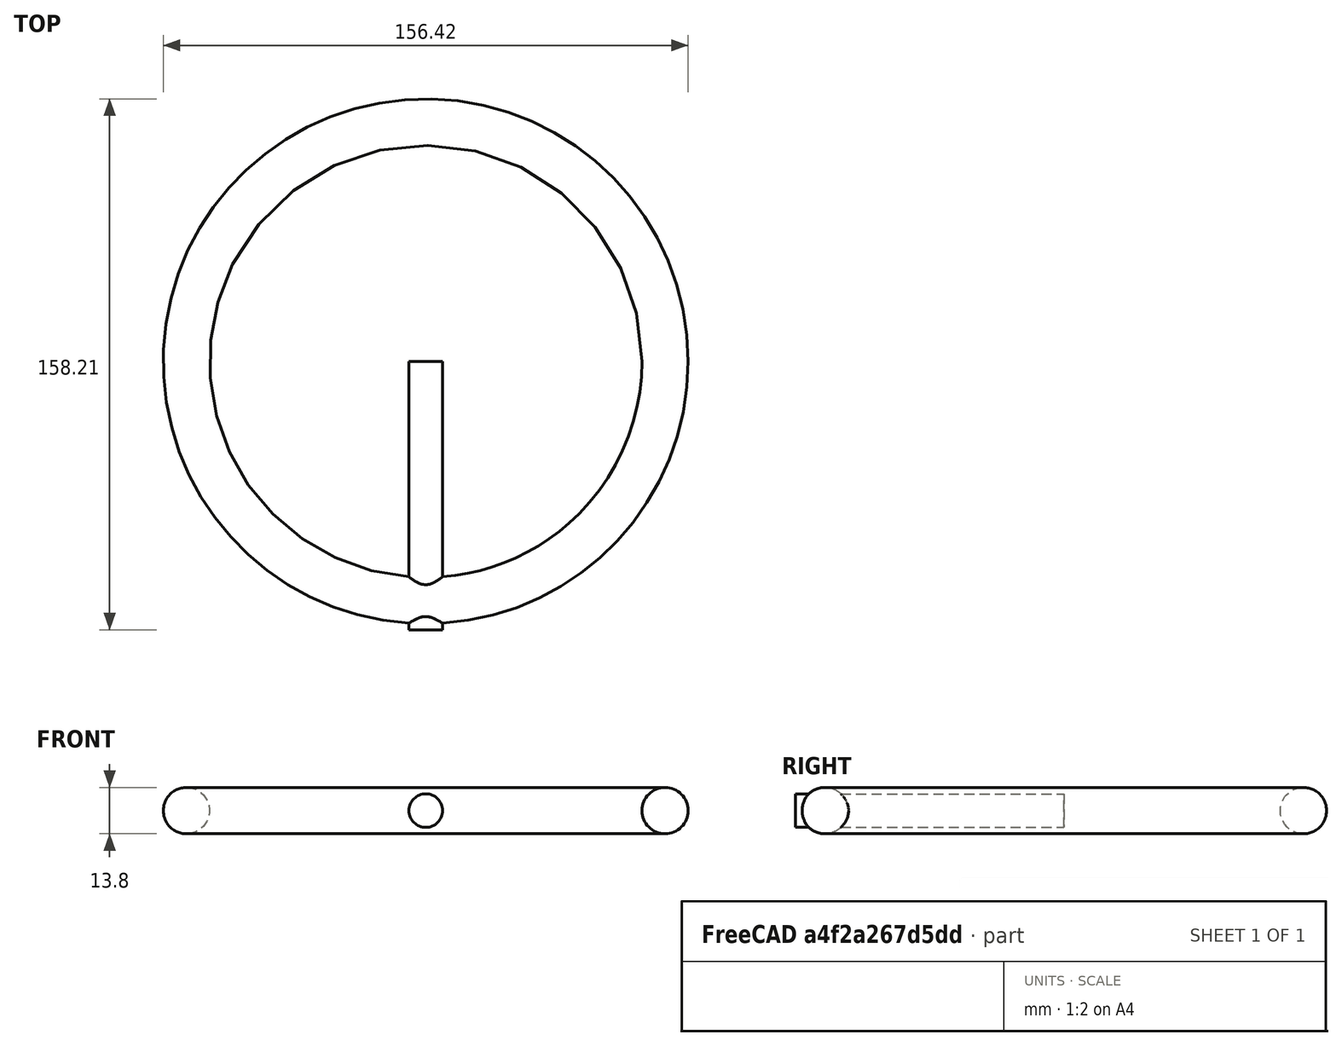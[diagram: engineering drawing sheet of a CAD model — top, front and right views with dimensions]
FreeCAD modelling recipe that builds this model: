
FCSTD DOCUMENT  (FreeCAD 0.21R33668 +26 (Git))
Label: Perçcage cylindre essai1
License: All rights reserved
LicenseURL: http://en.wikipedia.org/wiki/All_rights_reserved
objects: Sketcher::SketchObject×2, PartDesign::Revolution×1, PartDesign::Pad×1, PartDesign::Body×1, Part::Cut×1
note: 8 computed .brp shape members not serialized (recipe doc carries the construction recipe); baked Part::Feature solids carry a one-line shape summary decoded from their .brp

FEATURE [Sketcher::SketchObject] Sketch
  FullyConstrained = false
  MapMode = 5
  Placement = pos=(0,0,0) rot=(1,0,0;1.5708rad)
  Support = -> [XZ_Plane]
  sketch-geometry (1):
    g0: Circle CenterX=71.3094 CenterY=0 CenterZ=0 NormalX=0 NormalY=0 NormalZ=1 AngleXU=0 Radius=6.89621
  constraints (1):
    c: PointOnObject(g0,g-1)
FEATURE [PartDesign::Revolution] Revolution
  Angle = 360
  Axis = (0,-2e-16,1)
  Base = (0,0,0)
  Placement = pos=(0,0,0) rot=(1,0,0;1.5708rad)
  Profile = -> Sketch
  ReferenceAxis = -> Sketch [V_Axis]
  Reversed = true
FEATURE [Sketcher::SketchObject] Sketch001
  FullyConstrained = true
  MapMode = 5
  Placement = pos=(0,0,0) rot=(1,0,0;1.5708rad)
  Support = -> [XZ_Plane]
  sketch-geometry (1):
    g0: Circle CenterX=0 CenterY=0 CenterZ=0 NormalX=0 NormalY=0 NormalZ=1 AngleXU=0 Radius=5
  constraints (2):
    c: Coincident(g0,g-1)
    c: Radius(g0) = 5
FEATURE [PartDesign::Pad] Pad
  BaseFeature = -> Revolution
  Direction = (0,-1,-2e-16)
  Length = 80
  Length2 = 10
  Placement = pos=(0,0,0) rot=(1,0,0;1.5708rad)
  Profile = -> Sketch001
  ReferenceAxis = -> Sketch001 [N_Axis]
  Type = 0
FEATURE [PartDesign::Body] Body
  Group = -> [Sketch,Sketch001,Revolution,Pad]
  Origin = -> Origin
  Tip = -> Pad
FEATURE [Part::Cut] Cut001
  Base = -> Revolution
  Tool = -> Pad
